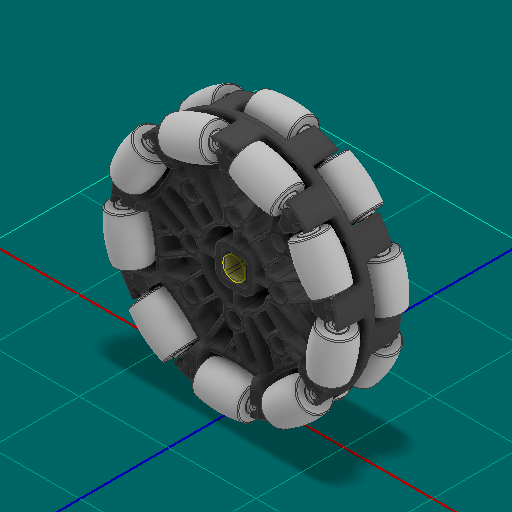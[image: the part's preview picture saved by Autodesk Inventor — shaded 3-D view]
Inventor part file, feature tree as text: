
AUTODESK INVENTOR PART (.ipt)
format: ipt  version: 2025 (Build 290162000, 162)  size: 28,580,864 bytes
history: native  units: in
note: dims shown in document units (in); Inventor stores cm internally (conversion verified against a paired STEP export)
features: other x59, sketch x1
ambient origin geometry x8: Origin, YZ Plane, XZ Plane, XY Plane, X Axis, Y Axis, Z Axis, Center Point
bodies: Solid1 (feature_tree), Solid2 (feature_tree), Solid3 (feature_tree), Solid4 (feature_tree), Solid5 (feature_tree), Solid6 (feature_tree), Solid7 (feature_tree), Solid8 (feature_tree), Solid9 (feature_tree), Solid10 (feature_tree), Solid11 (feature_tree), Solid12 (feature_tree), Solid13 (feature_tree), Solid14 (feature_tree), Solid15 (feature_tree), Solid16 (feature_tree), Solid17 (feature_tree), Solid18 (feature_tree), Solid19 (feature_tree), Solid20 (feature_tree), Solid21 (feature_tree), Solid22 (feature_tree), Solid23 (feature_tree), Solid24 (feature_tree), Solid25 (feature_tree), Solid26 (feature_tree), Solid27 (feature_tree), Solid28 (feature_tree), Solid29 (feature_tree), Solid30 (feature_tree), Solid31 (feature_tree), Solid32 (feature_tree), Solid33 (feature_tree), Solid34 (feature_tree), Solid35 (feature_tree), Solid36 (feature_tree), Solid37 (feature_tree), Solid38 (feature_tree), Solid39 (feature_tree), Solid40 (feature_tree), Solid41 (feature_tree), Solid42 (feature_tree), Solid43 (feature_tree), Solid44 (feature_tree), Solid45 (feature_tree), Solid46 (feature_tree), Solid47 (feature_tree), Solid48 (feature_tree), Solid49 (feature_tree), Solid50 (feature_tree), Solid51 (feature_tree), Solid52 (feature_tree), Solid53 (feature_tree), Solid54 (feature_tree), Solid55 (feature_tree)
feature tree (60):
  other  "2.75 Omni Antistatic.ipt"
  other  "Solid1::2.75 Omni Antistatic.ipt"
  other  "Solid2::2.75 Omni Antistatic.ipt"
  other  "Solid3::2.75 Omni Antistatic.ipt"
  other  "Solid4::2.75 Omni Antistatic.ipt"
  other  "Solid5::2.75 Omni Antistatic.ipt"
  other  "Solid6::2.75 Omni Antistatic.ipt"
  other  "Solid7::2.75 Omni Antistatic.ipt"
  other  "Solid8::2.75 Omni Antistatic.ipt"
  other  "Solid9::2.75 Omni Antistatic.ipt"
  other  "Solid10::2.75 Omni Antistatic.ipt"
  other  "Solid11::2.75 Omni Antistatic.ipt"
  other  "Solid12::2.75 Omni Antistatic.ipt"
  other  "Solid13::2.75 Omni Antistatic.ipt"
  other  "Solid14::2.75 Omni Antistatic.ipt"
  other  "Solid15::2.75 Omni Antistatic.ipt"
  other  "Solid16::2.75 Omni Antistatic.ipt"
  other  "Solid17::2.75 Omni Antistatic.ipt"
  other  "Solid18::2.75 Omni Antistatic.ipt"
  other  "Solid19::2.75 Omni Antistatic.ipt"
  other  "Solid20::2.75 Omni Antistatic.ipt"
  other  "Solid21::2.75 Omni Antistatic.ipt"
  other  "Solid22::2.75 Omni Antistatic.ipt"
  other  "Solid23::2.75 Omni Antistatic.ipt"
  other  "Solid24::2.75 Omni Antistatic.ipt"
  other  "Solid25::2.75 Omni Antistatic.ipt"
  other  "Solid26::2.75 Omni Antistatic.ipt"
  other  "Solid27::2.75 Omni Antistatic.ipt"
  other  "Solid28::2.75 Omni Antistatic.ipt"
  other  "Solid29::2.75 Omni Antistatic.ipt"
  other  "Solid30::2.75 Omni Antistatic.ipt"
  other  "Solid31::2.75 Omni Antistatic.ipt"
  other  "Solid32::2.75 Omni Antistatic.ipt"
  other  "Solid33::2.75 Omni Antistatic.ipt"
  other  "Solid34::2.75 Omni Antistatic.ipt"
  other  "Solid35::2.75 Omni Antistatic.ipt"
  other  "Solid36::2.75 Omni Antistatic.ipt"
  other  "Solid37::2.75 Omni Antistatic.ipt"
  other  "Solid38::2.75 Omni Antistatic.ipt"
  other  "Solid39::2.75 Omni Antistatic.ipt"
  other  "Solid40::2.75 Omni Antistatic.ipt"
  other  "Solid41::2.75 Omni Antistatic.ipt"
  other  "Solid42::2.75 Omni Antistatic.ipt"
  other  "Solid43::2.75 Omni Antistatic.ipt"
  other  "Solid44::2.75 Omni Antistatic.ipt"
  other  "Solid45::2.75 Omni Antistatic.ipt"
  other  "Solid46::2.75 Omni Antistatic.ipt"
  other  "Solid47::2.75 Omni Antistatic.ipt"
  other  "Solid48::2.75 Omni Antistatic.ipt"
  other  "Solid49::2.75 Omni Antistatic.ipt"
  other  "Solid50::2.75 Omni Antistatic.ipt"
  other  "Solid51::2.75 Omni Antistatic.ipt"
  other  "Solid52::2.75 Omni Antistatic.ipt"
  other  "Solid53::2.75 Omni Antistatic.ipt"
  other  "Solid54::2.75 Omni Antistatic.ipt"
  other  "Solid55::2.75 Omni Antistatic.ipt"
  other  "TaggingFeature1"
  sketch  "Sketch1"  dims[d0=0.3937in]
  other  "Srf1"
  other  "Srf1::Derived"
